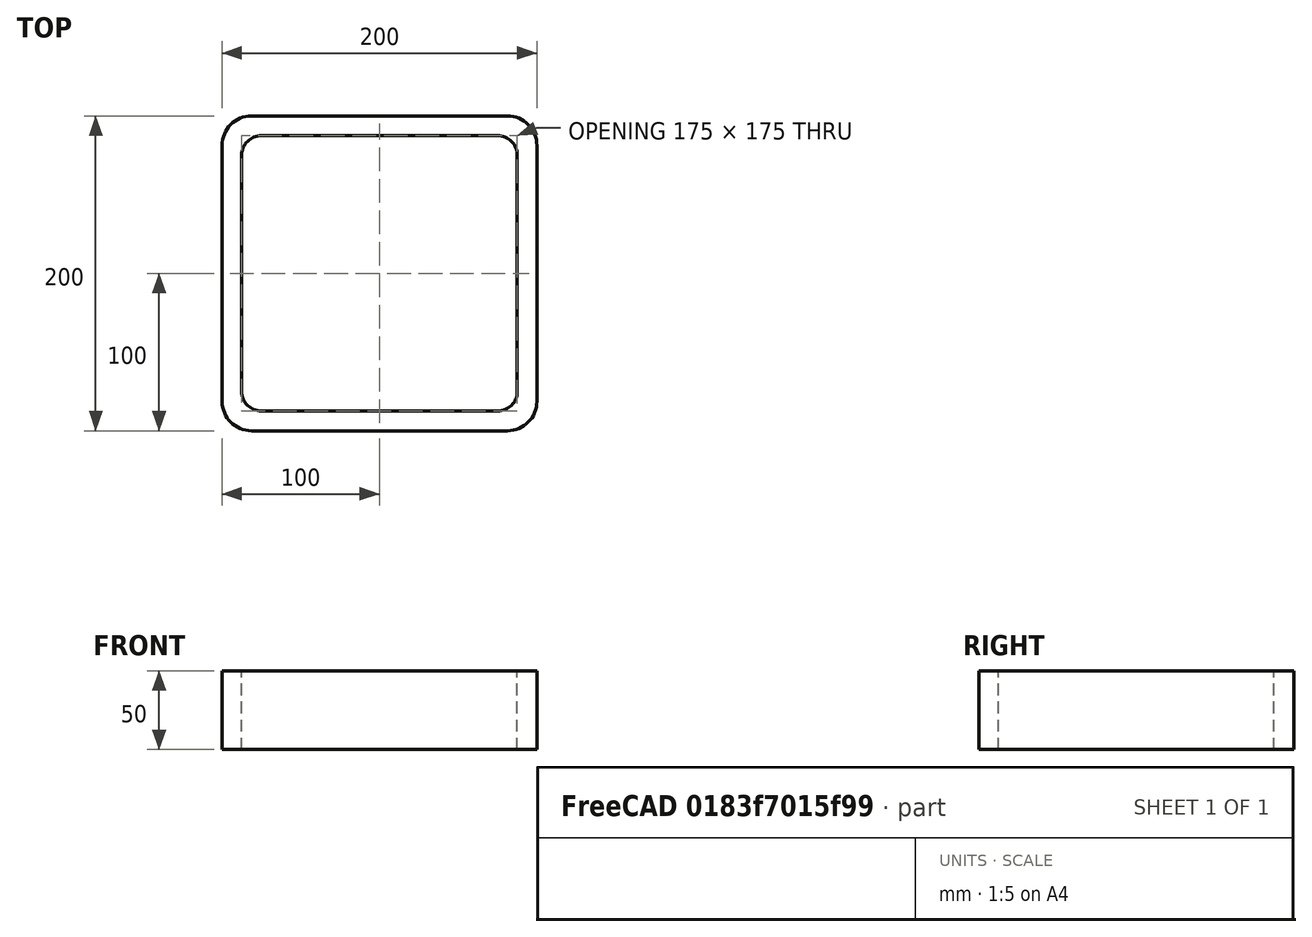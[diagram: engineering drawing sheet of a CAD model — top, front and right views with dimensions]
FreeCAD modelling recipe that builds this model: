
FCSTD DOCUMENT  (FreeCAD 0.15R4671 (Git))
Label: Square hollow section 200x200x12.5 EN10219 S235JRH
License: All rights reserved
LicenseURL: http://en.wikipedia.org/wiki/All_rights_reserved
objects: Sketcher::SketchObject×1, Part::Extrusion×1
note: 2 computed .brp shape members not serialized (recipe doc carries the construction recipe); baked Part::Feature solids carry a one-line shape summary decoded from their .brp

FEATURE [Sketcher::SketchObject] Sketch
  sketch-geometry (16):
    g0: LineSegment StartX=-75 StartY=87.5 StartZ=0 EndX=75 EndY=87.5 EndZ=0
    g1: LineSegment StartX=87.5 StartY=75 StartZ=0 EndX=87.5 EndY=-75 EndZ=0
    g2: LineSegment StartX=75 StartY=-87.5 StartZ=0 EndX=-75 EndY=-87.5 EndZ=0
    g3: LineSegment StartX=-87.5 StartY=-75 StartZ=0 EndX=-87.5 EndY=75 EndZ=0
    g4: LineSegment StartX=-81.25 StartY=100 StartZ=0 EndX=81.25 EndY=100 EndZ=0
    g5: LineSegment StartX=100 StartY=81.25 StartZ=0 EndX=100 EndY=-81.25 EndZ=0
    g6: LineSegment StartX=81.25 StartY=-100 StartZ=0 EndX=-81.25 EndY=-100 EndZ=0
    g7: LineSegment StartX=-100 StartY=-81.25 StartZ=0 EndX=-100 EndY=81.25 EndZ=0
    g8: ArcOfCircle CenterX=-75 CenterY=75 CenterZ=0 NormalX=0 NormalY=0 NormalZ=1 Radius=12.5 StartAngle=1.5708 EndAngle=3.14159
    g9: ArcOfCircle CenterX=75 CenterY=75 CenterZ=0 NormalX=0 NormalY=0 NormalZ=1 Radius=12.5 StartAngle=0 EndAngle=1.5708
    g10: ArcOfCircle CenterX=75 CenterY=-75 CenterZ=0 NormalX=0 NormalY=0 NormalZ=1 Radius=12.5 StartAngle=4.71239 EndAngle=6.28319
    g11: ArcOfCircle CenterX=-75 CenterY=-75 CenterZ=0 NormalX=0 NormalY=0 NormalZ=1 Radius=12.5 StartAngle=3.14159 EndAngle=4.71239
    g12: ArcOfCircle CenterX=81.25 CenterY=81.25 CenterZ=0 NormalX=0 NormalY=0 NormalZ=1 Radius=18.75 StartAngle=0 EndAngle=1.5708
    g13: ArcOfCircle CenterX=81.25 CenterY=-81.25 CenterZ=0 NormalX=0 NormalY=0 NormalZ=1 Radius=18.75 StartAngle=4.71239 EndAngle=6.28319
    g14: ArcOfCircle CenterX=-81.25 CenterY=-81.25 CenterZ=0 NormalX=0 NormalY=0 NormalZ=1 Radius=18.75 StartAngle=3.14159 EndAngle=4.71239
    g15: ArcOfCircle CenterX=-81.25 CenterY=81.25 CenterZ=0 NormalX=0 NormalY=0 NormalZ=1 Radius=18.75 StartAngle=1.5708 EndAngle=3.14159
  constraints (36):
    c: Horizontal(g2)
    c: Vertical(g3)
    c: Horizontal(g6)
    c: Vertical(g7)
    c: Tangent(g3,g8) = 1.5708
    c: Tangent(g0,g8) = 1.5708
    c: Tangent(g0,g9) = 1.5708
    c: Tangent(g1,g9) = 1.5708
    c: Tangent(g1,g10) = 1.5708
    c: Tangent(g2,g10) = 1.5708
    c: Tangent(g2,g11) = 1.5708
    c: Tangent(g3,g11) = 1.5708
    c: Tangent(g4,g12) = 1.5708
    c: Tangent(g5,g12) = 1.5708
    c: Tangent(g5,g13) = 1.5708
    c: Tangent(g6,g13) = 1.5708
    c: Tangent(g6,g14) = 1.5708
    c: Tangent(g7,g14) = 1.5708
    c: Tangent(g7,g15) = 1.5708
    c: Tangent(g4,g15) = 1.5708
    c: Equal(g9,g8)
    c: Equal(g9,g11)
    c: Equal(g9,g10)
    c: Equal(g12,g15)
    c: Equal(g12,g14)
    c: Equal(g12,g13)
    c: Symmetric(g4,g6,g-1)
    c: Symmetric(g7,g5,g-2)
    c: DistanceY(g4,g6) = -200
    c: DistanceX(g7,g5) = 200
    c: Symmetric(g3,g1,g-2)
    c: Symmetric(g0,g2,g-1)
    c: DistanceY(g0,g4) = 12.5
    c: DistanceX(g5,g1) = -12.5
    c: Radius(g9) = 12.5
    c: Radius(g12) = 18.75
FEATURE [Part::Extrusion] Extrude  label="Square hollow section 200x200x12.5 EN10219 S235JRH"
  Base = -> Sketch
  Dir = (0,0,50)
  Solid = true
